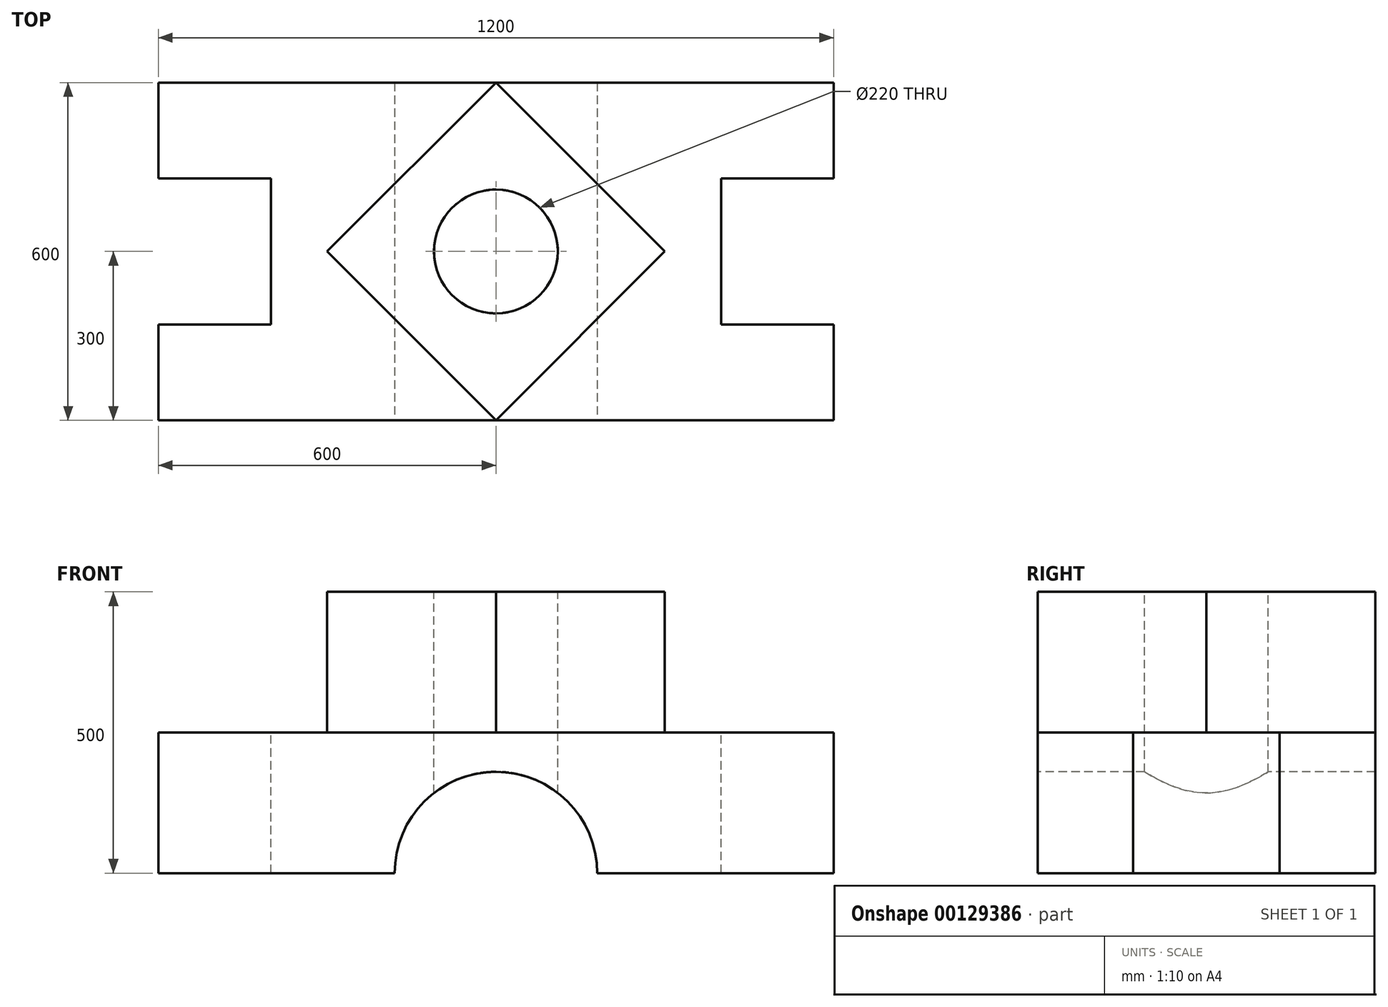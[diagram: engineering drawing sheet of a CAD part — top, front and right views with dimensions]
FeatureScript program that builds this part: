
annotation { "Feature Type Name" : "Feature", "Feature Type Description" : "" }
export const myFeature = defineFeature(function(context is Context, id is Id, definition is map)
    precondition{}
    {
        {
            var Q0;
            Q0=qCreatedBy(makeId("Top.planeOp"),FACE);
            var sketch = newSketch(context, id + "F0", { "sketchPlane" : qUnion([Q0])});
            skLineSegment(sketch, "E0.bottom", {"start": v(600, 300) * mm, "end": v(-600, 300) * mm});
            skLineSegment(sketch, "E0.top", {"start": v(600, -300) * mm, "end": v(-600, -300) * mm});
            skLineSegment(sketch, "E0.left", {"start": v(600, 300) * mm, "end": v(600, -300) * mm});
            skLineSegment(sketch, "E0.right", {"start": v(-600, 300) * mm, "end": v(-600, -300) * mm});
            skPoint(sketch, "E0.middle", {"position": v(0, 0) * mm});
            skSolve(sketch);
        }
        {
            var Q0;
            Q0=makeQuery(id+"F0.imprint","IMPRINT",FACE,{"disambiguationData":[TD([[makeQuery(id+"F0.imprint","IMPRINT",EDGE,{"derivedFrom":sQuery(id+"F0.wireOp",EDGE,"E0.bottom")}),1.0]])]});
            extrude(context, id + "F1", {"entities" : qUnion([Q0]), "depth" : 250 * mm});
        }
        {
            var Q0;
            Q0=makeQuery(id+"F1.opExtrude","CAP_FACE",FACE,{"disambiguationData":[OSD([sQuery(id+"F0.wireOp",EDGE,"E0.bottom"),sQuery(id+"F0.wireOp",EDGE,"E0.top"),sQuery(id+"F0.wireOp",EDGE,"E0.left"),sQuery(id+"F0.wireOp",EDGE,"E0.right")])],"isStart":false});
            var sketch = newSketch(context, id + "F2", { "sketchPlane" : qUnion([Q0])});
            skLineSegment(sketch, "E1.bottom", {"start": v(-400, 130) * mm, "end": v(-800, 130) * mm});
            skLineSegment(sketch, "E1.top", {"start": v(-400, -130) * mm, "end": v(-800, -130) * mm});
            skLineSegment(sketch, "E1.left", {"start": v(-400, 130) * mm, "end": v(-400, -130) * mm});
            skLineSegment(sketch, "E1.right", {"start": v(-800, 130) * mm, "end": v(-800, -130) * mm});
            skPoint(sketch, "E1.middle", {"position": v(-600, 0) * mm});
            skLineSegment(sketch, "E2", {"start": v(0, 300) * mm, "end": v(0, -300) * mm, "construction": true});
            skLineSegment(sketch, "E3.MirrorCS", {"start": v(400, 130) * mm, "end": v(800, 130) * mm});
            skLineSegment(sketch, "E4.MirrorCS", {"start": v(400, 130) * mm, "end": v(400, -130) * mm});
            skLineSegment(sketch, "E5.MirrorCS", {"start": v(400, -130) * mm, "end": v(800, -130) * mm});
            skLineSegment(sketch, "E6.MirrorCS", {"start": v(800, 130) * mm, "end": v(800, -130) * mm});
            skSolve(sketch);
        }
        {
            var Q0;
            {var subQ0=sQuery(id+"F2.wireOp",EDGE,"E1.right");Q0=makeQuery(id+"F2.imprint","IMPRINT",FACE,{"disambiguationData":[TD([[makeQuery(id+"F2.imprint","IMPRINT",EDGE,{"derivedFrom":subQ0}),1.0]])]});}
            var Q1;
            {var subQ0=sQuery(id+"F2.wireOp",EDGE,"E1.left");Q1=makeQuery(id+"F2.imprint","IMPRINT",FACE,{"disambiguationData":[TD([[makeQuery(id+"F2.imprint","IMPRINT",EDGE,{"derivedFrom":subQ0}),-1.0]])]});}
            var Q2;
            {var subQ0=sQuery(id+"F2.wireOp",EDGE,"E4.MirrorCS");Q2=makeQuery(id+"F2.imprint","IMPRINT",FACE,{"disambiguationData":[TD([[makeQuery(id+"F2.imprint","IMPRINT",EDGE,{"derivedFrom":subQ0}),1.0]])]});}
            extrude(context, id + "F3", {"entities" : qUnion([Q0, Q1, Q2]), "operationType" : NewBodyOperationType.REMOVE, "endBound" : BoundingType.THROUGH_ALL, "oppositeDirection" : true, "depth" : 25 * mm});
        }
        {
            var Q0;
            Q0=makeQuery(id+"F1.opExtrude","CAP_FACE",FACE,{"disambiguationData":[OSD([sQuery(id+"F0.wireOp",EDGE,"E0.bottom"),sQuery(id+"F0.wireOp",EDGE,"E0.top"),sQuery(id+"F0.wireOp",EDGE,"E0.left"),sQuery(id+"F0.wireOp",EDGE,"E0.right")])],"isStart":false});
            var sketch = newSketch(context, id + "F4", { "sketchPlane" : qUnion([Q0])});
            skLineSegment(sketch, "E7", {"start": v(0, 300) * mm, "end": v(-300, 0) * mm});
            skLineSegment(sketch, "E8", {"start": v(-300, 0) * mm, "end": v(0, -300) * mm});
            skLineSegment(sketch, "E9", {"start": v(0, -300) * mm, "end": v(300, 0) * mm});
            skLineSegment(sketch, "E10", {"start": v(300, 0) * mm, "end": v(0, 300) * mm});
            skSolve(sketch);
        }
        {
            var Q0;
            Q0=makeQuery(id+"F4.imprint","IMPRINT",FACE,{"disambiguationData":[TD([[makeQuery(id+"F4.imprint","IMPRINT",EDGE,{"derivedFrom":sQuery(id+"F4.wireOp",EDGE,"E7")}),1.0]])]});
            extrude(context, id + "F5", {"entities" : qUnion([Q0]), "operationType" : NewBodyOperationType.ADD, "depth" : 250 * mm});
        }
        {
            var Q0;
            Q0=makeQuery(id+"F5.opExtrude","CAP_FACE",FACE,{"disambiguationData":[OSD([sQuery(id+"F4.wireOp",EDGE,"E7"),sQuery(id+"F4.wireOp",EDGE,"E8"),sQuery(id+"F4.wireOp",EDGE,"E9"),sQuery(id+"F4.wireOp",EDGE,"E10")])],"isStart":false});
            var sketch = newSketch(context, id + "F6", { "sketchPlane" : qUnion([Q0])});
            skCircle(sketch, "E11", {"center": v(0, 0) * mm, "radius": 110 * mm});
            skSolve(sketch);
        }
        {
            var Q0;
            Q0=makeQuery(id+"F6.imprint","IMPRINT",FACE,{"disambiguationData":[TD([[makeQuery(id+"F6.imprint","IMPRINT",EDGE,{"derivedFrom":sQuery(id+"F6.wireOp",EDGE,"E11")}),1.0]])]});
            extrude(context, id + "F7", {"entities" : qUnion([Q0]), "operationType" : NewBodyOperationType.REMOVE, "endBound" : BoundingType.THROUGH_ALL, "oppositeDirection" : true, "depth" : 25 * mm});
        }
        {
            var Q0;
            Q0=makeQuery(id+"F1.opExtrude","SWEPT_FACE",FACE,{"disambiguationData":[OSD([sQuery(id+"F0.wireOp",EDGE,"E0.top")])]});
            var sketch = newSketch(context, id + "F8", { "sketchPlane" : qUnion([Q0])});
            skCircle(sketch, "E12", {"center": v(0, 0) * mm, "radius": 180 * mm});
            skSolve(sketch);
        }
        {
            var Q0;
            {var subQ0=sQuery(id+"F8.wireOp",EDGE,"E12");var subQ1=makeQuery(id+"F1.opExtrude","CAP_EDGE",EDGE,{"disambiguationData":[OSD([sQuery(id+"F0.wireOp",EDGE,"E0.top")])],"isStart":true});var subQ2=makeQuery(id+"F8.imprint","INTERSECT",VERTEX,{"disambiguationData":[OD(0.0)],"derivedFrom":[subQ1,subQ0]});Q0=makeQuery(id+"F8.imprint","IMPRINT",FACE,{"disambiguationData":[TD([[makeQuery(id+"F8.imprint","IMPRINT",EDGE,{"disambiguationData":[TD([[subQ2,-1.0]])],"derivedFrom":subQ0}),1.0]])]});}
            extrude(context, id + "F9", {"entities" : qUnion([Q0]), "operationType" : NewBodyOperationType.REMOVE, "endBound" : BoundingType.THROUGH_ALL, "oppositeDirection" : true, "depth" : 25 * mm});
        }
    });
